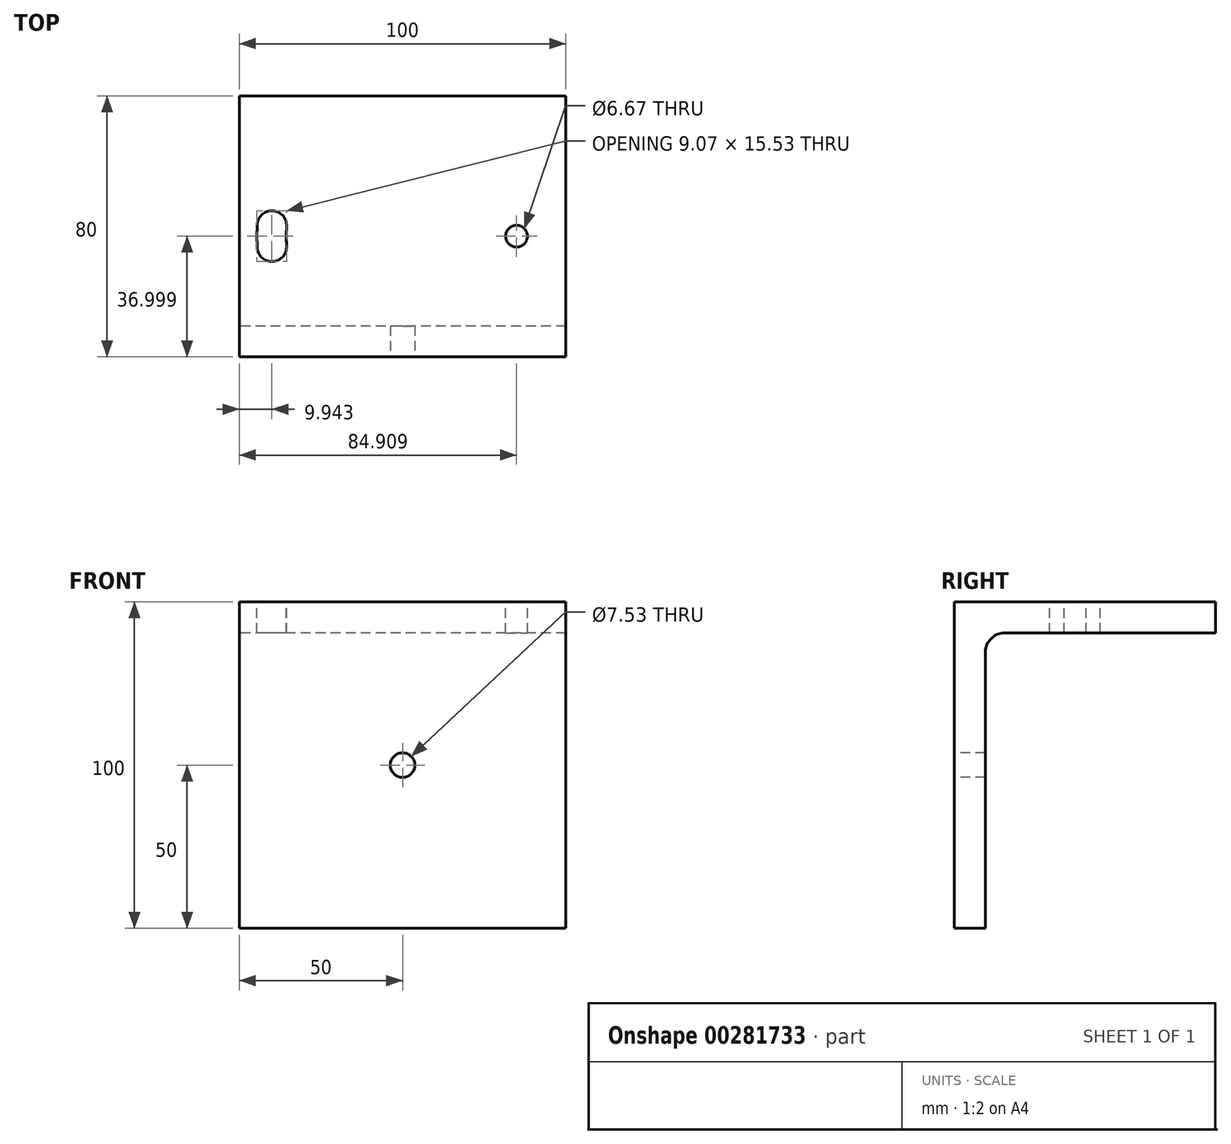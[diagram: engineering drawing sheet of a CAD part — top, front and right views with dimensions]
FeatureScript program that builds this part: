
annotation { "Feature Type Name" : "Feature", "Feature Type Description" : "" }
export const myFeature = defineFeature(function(context is Context, id is Id, definition is map)
    precondition{}
    {
        {
            var Q0;
            Q0=qCreatedBy(makeId("Right.planeOp"),FACE);
            var sketch = newSketch(context, id + "F0", { "sketchPlane" : qUnion([Q0])});
            skLineSegment(sketch, "E0", {"start": v(0, 0) * mm, "end": v(80, 0) * mm});
            skLineSegment(sketch, "E1", {"start": v(80, 0) * mm, "end": v(80, -9.5) * mm});
            skLineSegment(sketch, "E2", {"start": v(80, -9.5) * mm, "end": v(15.5, -9.5) * mm});
            skLineSegment(sketch, "E3", {"start": v(9.5, -15.5) * mm, "end": v(9.5, -100) * mm});
            skLineSegment(sketch, "E4", {"start": v(9.5, -100) * mm, "end": v(0, -100) * mm});
            skLineSegment(sketch, "E5", {"start": v(0, -100) * mm, "end": v(0, 0) * mm});
            skPoint(sketch, "E6.visualSharp", {"position": v(9.5, -9.5) * mm});
            skArc(sketch, "E6.filletArc", {"start": v(15.5, -9.5) * mm, "mid": v(11.26, -11.26) * mm, "end": v(9.5, -15.5) * mm});
            skSolve(sketch);
        }
        {
            var Q0;
            Q0=makeQuery(id+"F0.imprint","IMPRINT",FACE,{"disambiguationData":[TD([[makeQuery(id+"F0.imprint","IMPRINT",EDGE,{"derivedFrom":sQuery(id+"F0.wireOp",EDGE,"E0")}),-1.0]])]});
            extrude(context, id + "F1", {"entities" : qUnion([Q0]), "depth" : 100 * mm});
        }
        {
            var Q0;
            Q0=makeQuery(id+"F1.opExtrude","SWEPT_FACE",FACE,{"disambiguationData":[OSD([sQuery(id+"F0.wireOp",EDGE,"E0")])]});
            var sketch = newSketch(context, id + "F2", { "sketchPlane" : qUnion([Q0])});
            skPoint(sketch, "E7", {"position": v(84.9, 37) * mm});
            skCircle(sketch, "E8", {"center": v(84.9, 37) * mm, "radius": 3.33 * mm});
            skArc(sketch, "E9.0.endCap", {"start": v(14.48, 33.92) * mm, "mid": v(10.18, 29.23) * mm, "end": v(5.48, 33.53) * mm});
            skArc(sketch, "E9.0.left", {"start": v(14.4, 37) * mm, "mid": v(14.43, 35.46) * mm, "end": v(14.48, 33.92) * mm});
            skArc(sketch, "E9.0.right", {"start": v(5.4, 37) * mm, "mid": v(5.43, 35.27) * mm, "end": v(5.48, 33.53) * mm});
            skArc(sketch, "E9.1.endCap", {"start": v(5.48, 40.47) * mm, "mid": v(10.18, 44.77) * mm, "end": v(14.48, 40.07) * mm});
            skArc(sketch, "E9.1.left", {"start": v(5.4, 37) * mm, "mid": v(5.43, 38.73) * mm, "end": v(5.48, 40.47) * mm});
            skArc(sketch, "E9.1.right", {"start": v(14.4, 37) * mm, "mid": v(14.43, 38.54) * mm, "end": v(14.48, 40.07) * mm});
            skSolve(sketch);
        }
        {
            var Q0;
            Q0=qSketchRegion(id+"F2",true);
            extrude(context, id + "F3", {"entities" : qUnion([Q0]), "operationType" : NewBodyOperationType.REMOVE, "oppositeDirection" : true, "depth" : 25 * mm});
        }
        {
            var Q0;
            Q0=makeQuery(id+"F1.opExtrude","SWEPT_FACE",FACE,{"disambiguationData":[OSD([sQuery(id+"F0.wireOp",EDGE,"E5")])]});
            var sketch = newSketch(context, id + "F4", { "sketchPlane" : qUnion([Q0])});
            skLineSegment(sketch, "E10", {"start": v(0, 0) * mm, "end": v(100, -100) * mm, "construction": true});
            skLineSegment(sketch, "E11", {"start": v(100, 0) * mm, "end": v(0, -100) * mm, "construction": true});
            skCircle(sketch, "E12", {"center": v(50, -50) * mm, "radius": 3.76 * mm});
            skSolve(sketch);
        }
        {
            var Q0;
            Q0=makeQuery(id+"F4.imprint","IMPRINT",FACE,{"disambiguationData":[TD([[makeQuery(id+"F4.imprint","IMPRINT",EDGE,{"derivedFrom":sQuery(id+"F4.wireOp",EDGE,"E12")}),1.0]])]});
            extrude(context, id + "F5", {"entities" : qUnion([Q0]), "operationType" : NewBodyOperationType.REMOVE, "oppositeDirection" : true, "depth" : 25 * mm, "offsetDistance" : 25 * mm});
        }
    });
